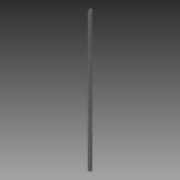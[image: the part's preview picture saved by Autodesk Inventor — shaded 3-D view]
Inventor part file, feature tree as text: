
AUTODESK INVENTOR PART (.ipt)
format: ipt  version: 2015 SP1 (Build 190203100, 203)  size: 104,960 bytes
history: native  units: mm
features: other x3, sketch x3
ambient origin geometry x8: Origin, YZ Plane, XZ Plane, XY Plane, X Axis, Y Axis, Z Axis, Center Point
bodies: Solid1 (feature_tree)
feature tree (6):
  other  "Poutre.ipt"
  other  "Solid1::Poutre.ipt"
  other  "TaggingFeature1"
  sketch  "Sketch1"  dims[d0=10.0mm]
  sketch  "Sketch2"
  sketch  "Sketch3"
